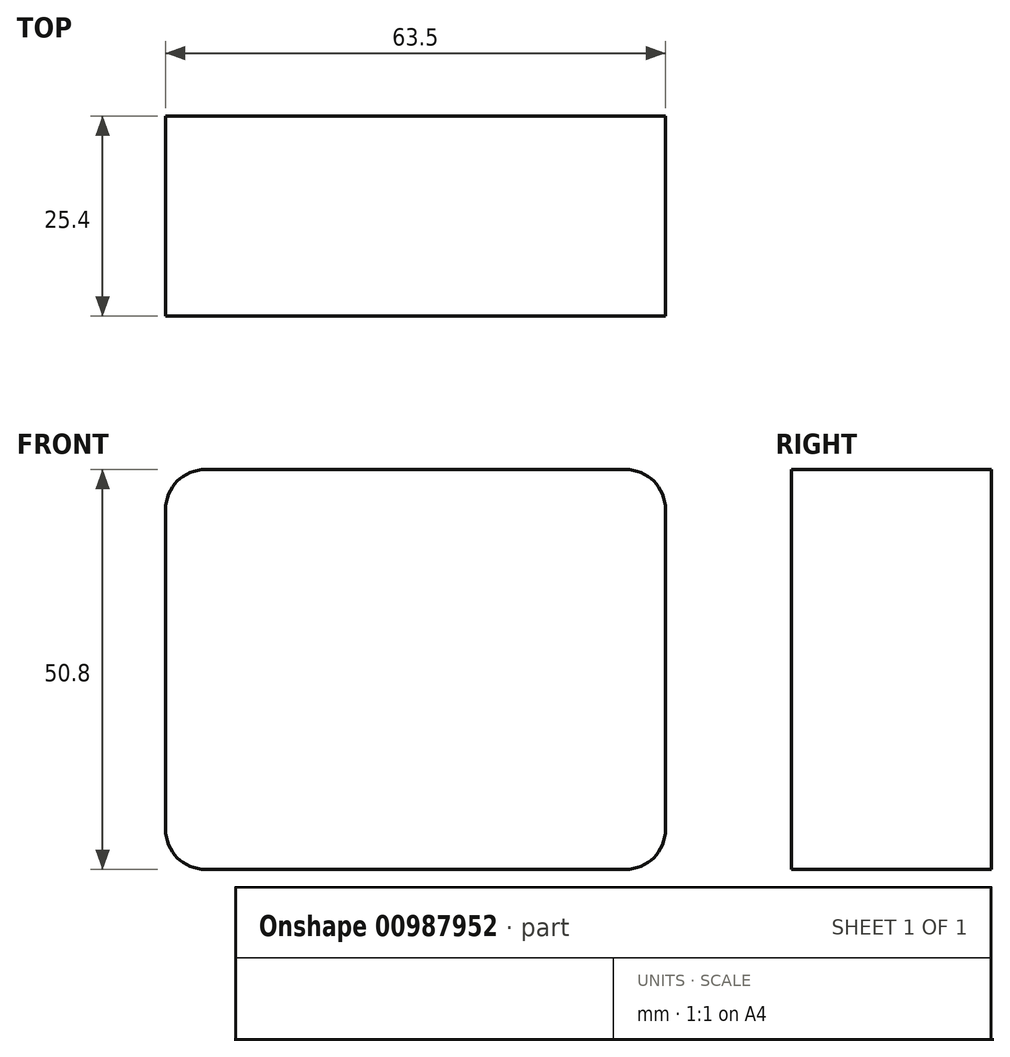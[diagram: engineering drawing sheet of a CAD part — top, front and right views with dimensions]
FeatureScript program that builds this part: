
annotation { "Feature Type Name" : "Feature", "Feature Type Description" : "" }
export const myFeature = defineFeature(function(context is Context, id is Id, definition is map)
    precondition{}
    {
        {
            var Q0;
            Q0=qCreatedBy(makeId("Front.planeOp"),FACE);
            var sketch = newSketch(context, id + "F0", { "sketchPlane" : qUnion([Q0])});
            skLineSegment(sketch, "E0.bottom", {"start": v(31.75, -25.4) * mm, "end": v(-31.75, -25.4) * mm});
            skLineSegment(sketch, "E0.top", {"start": v(31.75, 25.4) * mm, "end": v(-31.75, 25.4) * mm});
            skLineSegment(sketch, "E0.left", {"start": v(31.75, -25.4) * mm, "end": v(31.75, 25.4) * mm});
            skLineSegment(sketch, "E0.right", {"start": v(-31.75, -25.4) * mm, "end": v(-31.75, 25.4) * mm});
            skPoint(sketch, "E0.middle", {"position": v(0, 0) * mm});
            skSolve(sketch);
        }
        {
            var Q0;
            Q0 = qSketchRegion(id + "F0", true);
            extrude(context, id + "F1", {"entities" : qUnion([Q0]), "endBound" : BoundingType.SYMMETRIC, "depth" : 25.4 * mm, "offsetDistance" : 25.4 * mm});
        }
        {
            var Q0;
            Q0=makeQuery(id+"F1.opExtrude","SWEPT_EDGE",EDGE,{"disambiguationData":[OSD([sQuery(id+"F0.wireOp",EDGE,"E0.top"),sQuery(id+"F0.wireOp",EDGE,"E0.left")])]});
            var Q1;
            Q1=makeQuery(id+"F1.opExtrude","SWEPT_EDGE",EDGE,{"disambiguationData":[OSD([sQuery(id+"F0.wireOp",EDGE,"E0.top"),sQuery(id+"F0.wireOp",EDGE,"E0.right")])]});
            var Q2;
            Q2=makeQuery(id+"F1.opExtrude","SWEPT_EDGE",EDGE,{"disambiguationData":[OSD([sQuery(id+"F0.wireOp",EDGE,"E0.bottom"),sQuery(id+"F0.wireOp",EDGE,"E0.left")])]});
            var Q3;
            Q3=makeQuery(id+"F1.opExtrude","SWEPT_EDGE",EDGE,{"disambiguationData":[OSD([sQuery(id+"F0.wireOp",EDGE,"E0.bottom"),sQuery(id+"F0.wireOp",EDGE,"E0.right")])]});
            fillet(context, id + "F2", {"entities" : qUnion([Q0, Q1, Q2, Q3]), "radius" : 5.08 * mm, "tangentPropagation" : true, "allowEdgeOverflow" : false});
        }
    });
